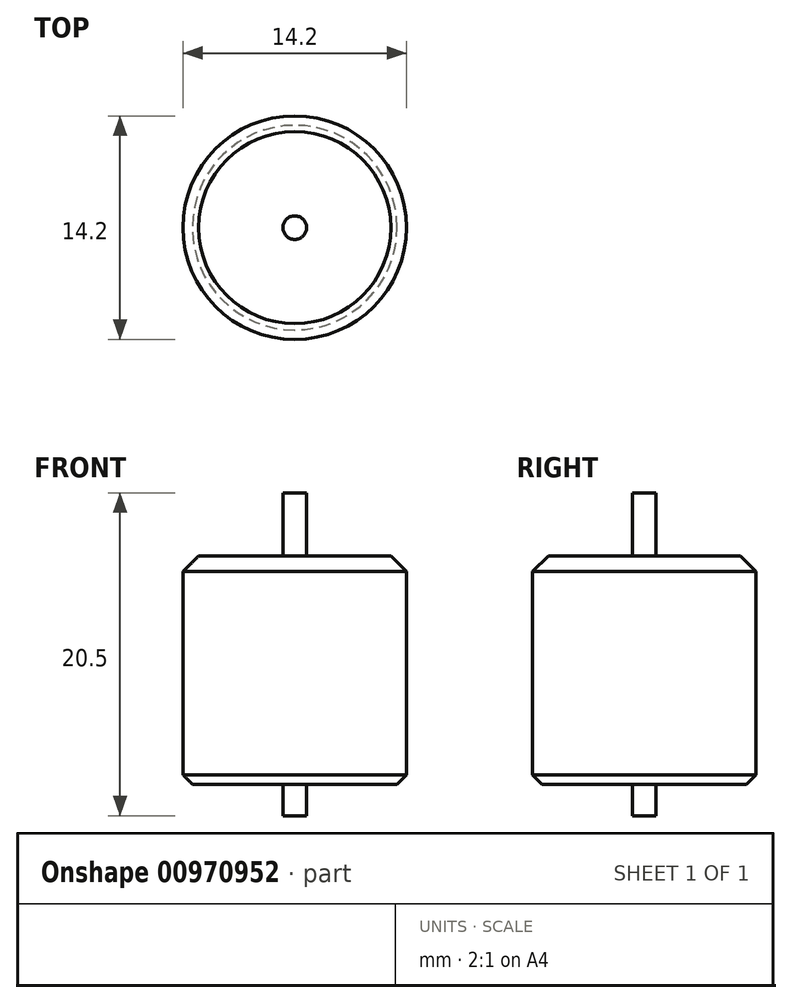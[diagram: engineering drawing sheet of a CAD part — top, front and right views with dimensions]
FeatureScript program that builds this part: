
annotation { "Feature Type Name" : "Feature", "Feature Type Description" : "" }
export const myFeature = defineFeature(function(context is Context, id is Id, definition is map)
    precondition{}
    {
        {
            var Q0;
            Q0=qCreatedBy(makeId("Front.planeOp"),FACE);
            var sketch = newSketch(context, id + "F0", { "sketchPlane" : qUnion([Q0])});
            skLineSegment(sketch, "E0.bottom", {"start": v(-0.75, 0) * mm, "end": v(-6.5, 0) * mm});
            skLineSegment(sketch, "E0.top", {"start": v(-0.75, 14.5) * mm, "end": v(-6.1, 14.5) * mm});
            skLineSegment(sketch, "E0.left", {"start": v(0, -2) * mm, "end": v(0, 18.5) * mm});
            skLineSegment(sketch, "E0.right", {"start": v(-7.1, 0.6) * mm, "end": v(-7.1, 13.5) * mm});
            skLineSegment(sketch, "E1", {"start": v(-0.75, 14.5) * mm, "end": v(-0.75, 18.5) * mm});
            skLineSegment(sketch, "E2", {"start": v(-0.75, 18.5) * mm, "end": v(0, 18.5) * mm});
            skLineSegment(sketch, "E3", {"start": v(-0.75, 14.5) * mm, "end": v(-0.75, 0) * mm, "construction": true});
            skLineSegment(sketch, "E4", {"start": v(-0.75, 0) * mm, "end": v(-0.75, -2) * mm});
            skLineSegment(sketch, "E5", {"start": v(-0.75, -2) * mm, "end": v(0, -2) * mm});
            skLineSegment(sketch, "E6", {"start": v(-7.1, 13.5) * mm, "end": v(-6.1, 14.5) * mm});
            skLineSegment(sketch, "E7", {"start": v(-7.1, 0.6) * mm, "end": v(-6.5, 0) * mm});
            skSolve(sketch);
        }
        {
            var Q0;
            Q0=makeQuery(id+"F0.imprint","IMPRINT",FACE,{"disambiguationData":[TD([[makeQuery(id+"F0.imprint","IMPRINT",EDGE,{"derivedFrom":sQuery(id+"F0.wireOp",EDGE,"E0.bottom")}),-1.0]])]});
            var Q1;
            Q1=sQuery(id+"F0.wireOp",EDGE,"E0.left");
            revolve(context, id + "F1", {"surfaceOperationType" : NewSurfaceOperationType.NEW, "entities" : qUnion([Q0]), "axis" : qUnion([Q1]), "revolveType" : RevolveType.FULL});
        }
    });
